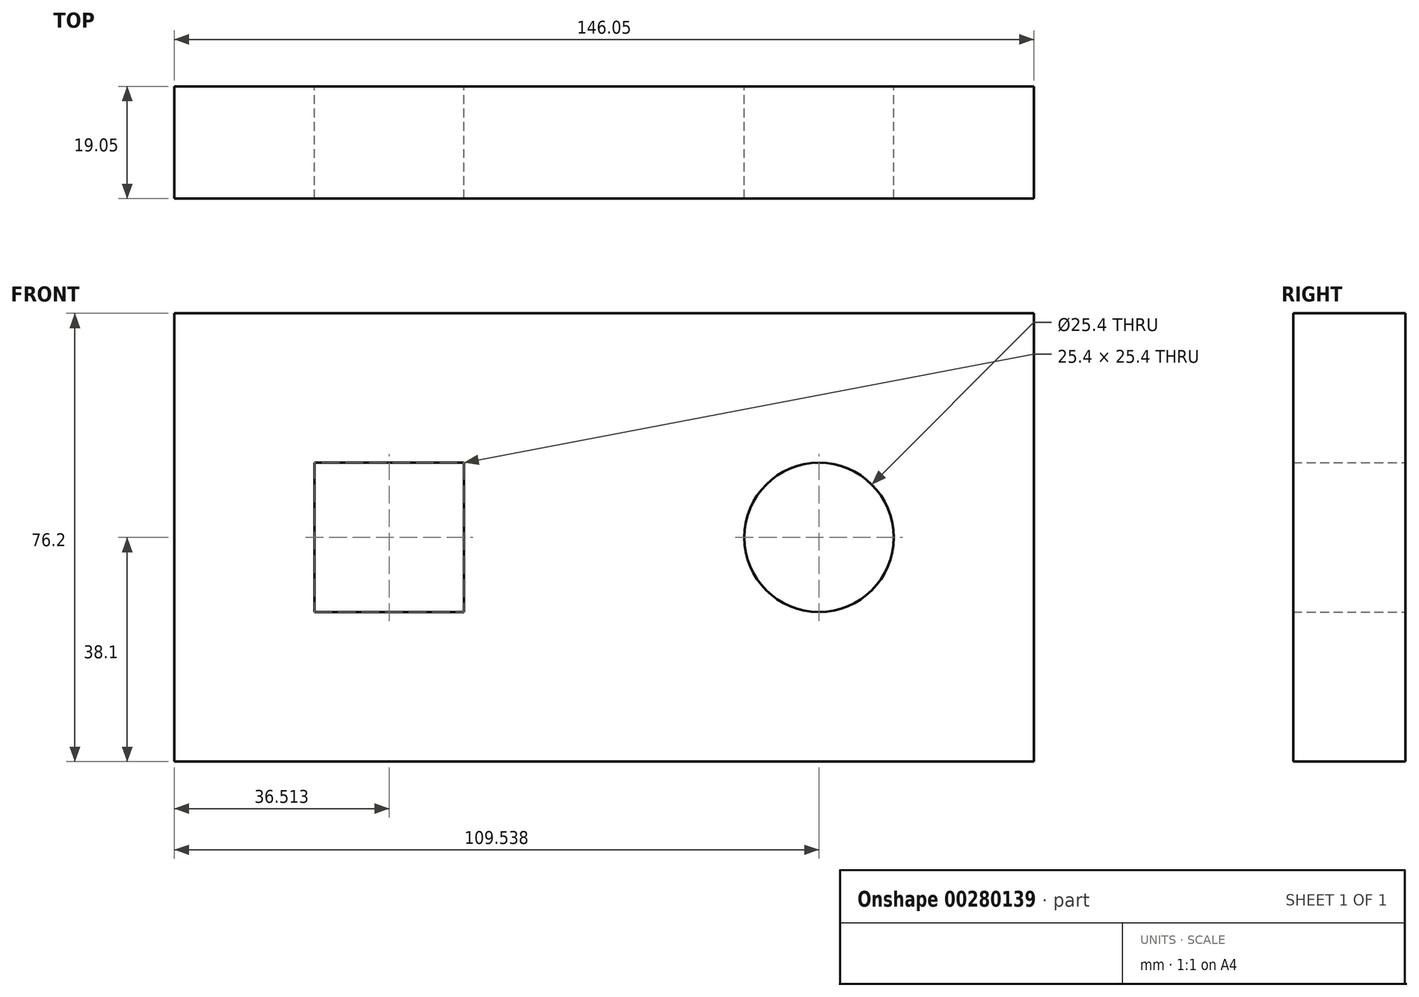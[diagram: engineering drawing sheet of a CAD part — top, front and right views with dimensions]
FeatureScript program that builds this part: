
annotation { "Feature Type Name" : "Feature", "Feature Type Description" : "" }
export const myFeature = defineFeature(function(context is Context, id is Id, definition is map)
    precondition{}
    {
        {
            var Q0;
            Q0=qCreatedBy(makeId("Front.planeOp"),FACE);
            var sketch = newSketch(context, id + "F0", { "sketchPlane" : qUnion([Q0])});
            skLineSegment(sketch, "E0.bottom", {"start": v(0, 0) * mm, "end": v(-146.05, 0) * mm});
            skLineSegment(sketch, "E0.top", {"start": v(0, 76.2) * mm, "end": v(-146.05, 76.2) * mm});
            skLineSegment(sketch, "E0.left", {"start": v(0, 0) * mm, "end": v(0, 76.2) * mm});
            skLineSegment(sketch, "E0.right", {"start": v(-146.05, 0) * mm, "end": v(-146.05, 76.2) * mm});
            skCircle(sketch, "E1", {"center": v(-36.51, 38.1) * mm, "radius": 12.7 * mm});
            skLineSegment(sketch, "E2.bottom", {"start": v(-122.24, 25.4) * mm, "end": v(-96.84, 25.4) * mm});
            skLineSegment(sketch, "E2.top", {"start": v(-122.24, 50.8) * mm, "end": v(-96.84, 50.8) * mm});
            skLineSegment(sketch, "E2.left", {"start": v(-122.24, 25.4) * mm, "end": v(-122.24, 50.8) * mm});
            skLineSegment(sketch, "E2.right", {"start": v(-96.84, 25.4) * mm, "end": v(-96.84, 50.8) * mm});
            skSolve(sketch);
        }
        {
            var Q0;
            Q0 = qSketchRegion(id + "F0", true);
            extrude(context, id + "F1", {"entities" : qUnion([Q0]), "depth" : 19.05 * mm});
        }
    });
